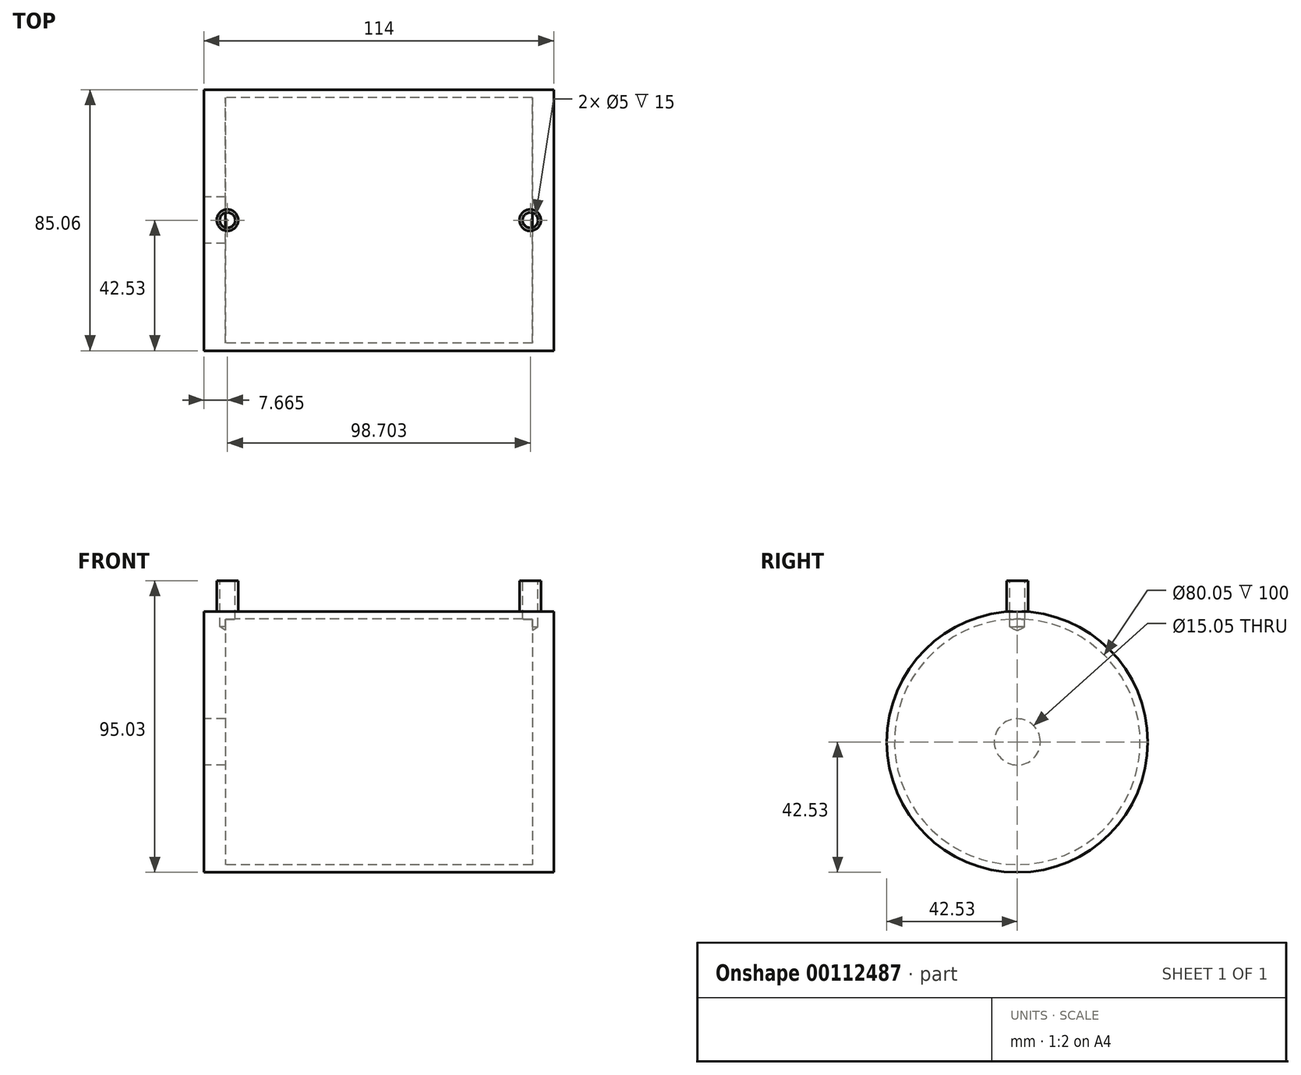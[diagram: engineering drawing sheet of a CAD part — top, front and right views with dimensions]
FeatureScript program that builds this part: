
annotation { "Feature Type Name" : "Feature", "Feature Type Description" : "" }
export const myFeature = defineFeature(function(context is Context, id is Id, definition is map)
    precondition{}
    {
        {
            var Q0;
            Q0=qCreatedBy(makeId("Right.planeOp"),FACE);
            var sketch = newSketch(context, id + "F0", { "sketchPlane" : qUnion([Q0])});
            skCircle(sketch, "E0", {"center": v(0, 0) * mm, "radius": 40.02 * mm});
            skCircle(sketch, "E1", {"center": v(0, 0) * mm, "radius": 42.52 * mm});
            skSolve(sketch);
        }
        {
            var Q0;
            Q0=makeQuery(id+"F0.imprint","IMPRINT",FACE,{"disambiguationData":[TD([[makeQuery(id+"F0.imprint","IMPRINT",EDGE,{"derivedFrom":sQuery(id+"F0.wireOp",EDGE,"E0")}),-1.0]])]});
            extrude(context, id + "F1", {"entities" : qUnion([Q0]), "endBound" : BoundingType.SYMMETRIC, "depth" : 100 * mm});
        }
        {
            var Q0;
            Q0=makeQuery(id+"F1.opExtrude","CAP_FACE",FACE,{"disambiguationData":[OSD([sQuery(id+"F0.wireOp",EDGE,"E0"),sQuery(id+"F0.wireOp",EDGE,"E1")])],"isStart":false});
            var sketch = newSketch(context, id + "F2", { "sketchPlane" : qUnion([Q0])});
            skCircle(sketch, "E2", {"center": v(0, 0) * mm, "radius": 42.52 * mm});
            skSolve(sketch);
        }
        {
            var Q0;
            Q0 = qSketchRegion(id + "F2", true);
            extrude(context, id + "F3", {"entities" : qUnion([Q0]), "depth" : 7 * mm});
        }
        {
            var Q0;
            Q0=makeQuery(id+"F3.opExtrude","SWEPT_BODY",BODY,{"disambiguationData":[OSD([sQuery(id+"F2.wireOp",EDGE,"E2")])]});
            var Q1;
            Q1=qCreatedBy(makeId("Right.planeOp"),FACE);
            mirror(context, id + "F4", {"operationType" : NewBodyOperationType.ADD, "entities" : qUnion([Q0]), "mirrorPlane" : qUnion([Q1])});
        }
        {
            var Q0;
            Q0=makeQuery(id+"F4.opPattern","COPY",FACE,{"derivedFrom":makeQuery(id+"F3.opExtrude","CAP_FACE",FACE,{"disambiguationData":[OSD([sQuery(id+"F2.wireOp",EDGE,"E2")])],"isStart":false}),"instanceName":"1"});
            var sketch = newSketch(context, id + "F5", { "sketchPlane" : qUnion([Q0])});
            skCircle(sketch, "E3", {"center": v(0, 0) * mm, "radius": 7.53 * mm});
            skSolve(sketch);
        }
        {
            var Q0;
            Q0=sQuery(id+"F5.wireOp",VERTEX,"E3.center");
            var Q1;
            Q1=makeQuery(id+"F1.opExtrude","SWEPT_BODY",BODY,{"disambiguationData":[OSD([sQuery(id+"F0.wireOp",EDGE,"E0"),sQuery(id+"F0.wireOp",EDGE,"E1")])]});
            hole(context, id + "F6", {"style" : HoleStyle.SIMPLE, "endStyle" : HoleEndStyle.BLIND, "holeDiameter" : 15.05 * mm, "holeDepth" : 12 * mm, "locations" : qUnion([Q0]), "scope" : qUnion([Q1])});
        }
        {
            var Q0;
            Q0=qCreatedBy(makeId("Top.planeOp"),FACE);
            cPlane(context, id + "F7", {"entities" : qUnion([Q0]), "cplaneType" : CPlaneType.OFFSET, "offset" : 42.5 * mm, "width" : 150 * mm, "height" : 150 * mm});
        }
        {
            var Q0;
            Q0=qCreatedBy(id+"F7.planeOp",FACE);
            var sketch = newSketch(context, id + "F8", { "sketchPlane" : qUnion([Q0])});
            skCircle(sketch, "E4", {"center": v(-49.33, 0) * mm, "radius": 3.5 * mm});
            skCircle(sketch, "E5.MirrorC", {"center": v(49.33, 0) * mm, "radius": 3.5 * mm});
            skSolve(sketch);
        }
        {
            var Q0;
            Q0 = qSketchRegion(id + "F8", true);
            extrude(context, id + "F9", {"entities" : qUnion([Q0]), "operationType" : NewBodyOperationType.ADD, "depth" : 10 * mm});
        }
        {
            var Q0;
            Q0=makeQuery(id+"F9.opExtrude","CAP_FACE",FACE,{"disambiguationData":[OSD([sQuery(id+"F8.wireOp",EDGE,"E4")])],"isStart":false});
            var sketch = newSketch(context, id + "F10", { "sketchPlane" : qUnion([Q0])});
            skPoint(sketch, "E6", {"position": v(-49.33, 0) * mm});
            skPoint(sketch, "E7", {"position": v(49.37, 0) * mm});
            skSolve(sketch);
        }
        {
            var Q0;
            Q0=sQuery(id+"F10.wireOp",VERTEX,"E6");
            var Q1;
            Q1=sQuery(id+"F10.wireOp",VERTEX,"E7");
            var Q2;
            Q2=makeQuery(id+"F1.opExtrude","SWEPT_BODY",BODY,{"disambiguationData":[OSD([sQuery(id+"F0.wireOp",EDGE,"E0"),sQuery(id+"F0.wireOp",EDGE,"E1")])]});
            hole(context, id + "F11", {"style" : HoleStyle.SIMPLE, "endStyle" : HoleEndStyle.BLIND, "holeDiameter" : 5 * mm, "holeDepth" : 15 * mm, "locations" : qUnion([Q0, Q1]), "scope" : qUnion([Q2])});
        }
    });
